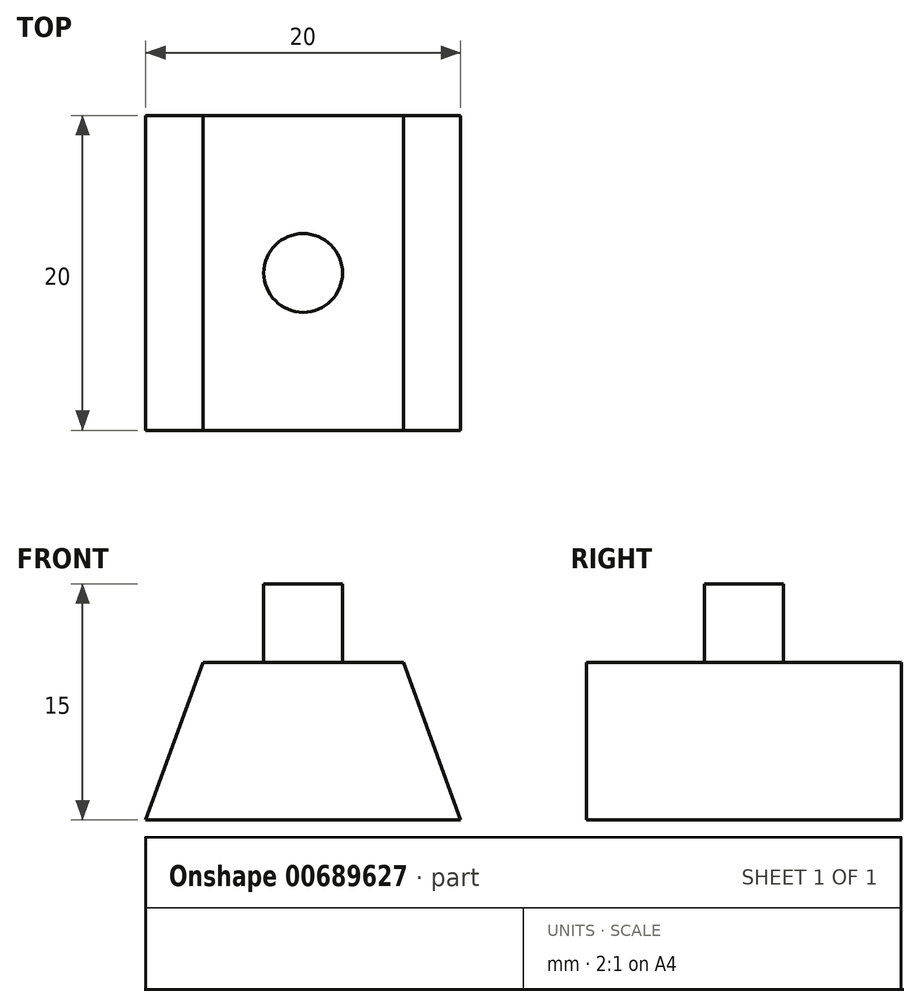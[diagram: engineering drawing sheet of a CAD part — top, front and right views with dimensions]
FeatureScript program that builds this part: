
annotation { "Feature Type Name" : "Feature", "Feature Type Description" : "" }
export const myFeature = defineFeature(function(context is Context, id is Id, definition is map)
    precondition{}
    {
        {
            var Q0;
            Q0=qCreatedBy(makeId("Front.planeOp"),FACE);
            var sketch = newSketch(context, id + "F0", { "sketchPlane" : qUnion([Q0])});
            skLineSegment(sketch, "E0", {"start": v(0, 0) * mm, "end": v(-20, 0) * mm});
            skLineSegment(sketch, "E1", {"start": v(-16.36, 10) * mm, "end": v(-3.64, 10) * mm});
            skLineSegment(sketch, "E2", {"start": v(-20, 0) * mm, "end": v(-16.36, 10) * mm});
            skLineSegment(sketch, "E3", {"start": v(-3.64, 10) * mm, "end": v(0, 0) * mm});
            skSolve(sketch);
        }
        {
            var Q0;
            Q0=makeQuery(id+"F0.imprint","IMPRINT",FACE,{"disambiguationData":[TD([[makeQuery(id+"F0.imprint","IMPRINT",EDGE,{"derivedFrom":sQuery(id+"F0.wireOp",EDGE,"E0")}),-1.0]])]});
            extrude(context, id + "F1", {"entities" : qUnion([Q0]), "depth" : 20 * mm, "offsetDistance" : 25 * mm});
        }
        {
            var Q0;
            Q0=qCreatedBy(makeId("Top.planeOp"),FACE);
            var sketch = newSketch(context, id + "F2", { "sketchPlane" : qUnion([Q0])});
            skLineSegment(sketch, "E4", {"start": v(0, 0) * mm, "end": v(0, -10) * mm});
            skLineSegment(sketch, "E5", {"start": v(0, -10) * mm, "end": v(-10, -10) * mm});
            skCircle(sketch, "E6", {"center": v(-10, -10) * mm, "radius": 2.5 * mm});
            skSolve(sketch);
        }
        {
            var Q0;
            Q0 = qSketchRegion(id + "F2", true);
            extrude(context, id + "F3", {"entities" : qUnion([Q0]), "operationType" : NewBodyOperationType.ADD, "depth" : 15 * mm, "offsetDistance" : 25 * mm});
        }
    });
